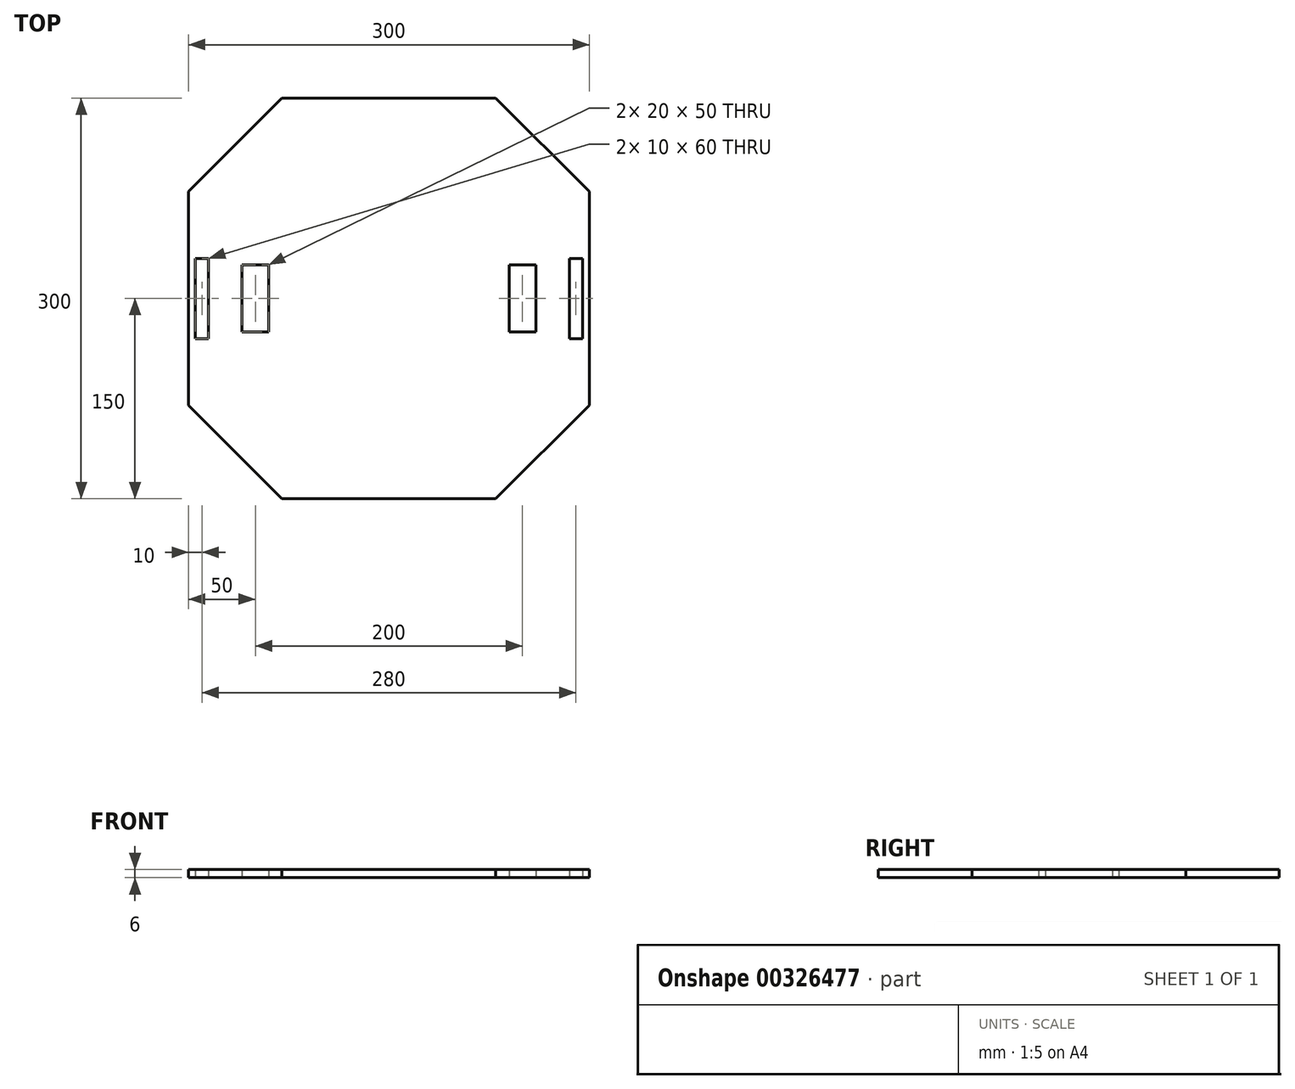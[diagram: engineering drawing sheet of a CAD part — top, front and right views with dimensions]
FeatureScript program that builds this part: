
annotation { "Feature Type Name" : "Feature", "Feature Type Description" : "" }
export const myFeature = defineFeature(function(context is Context, id is Id, definition is map)
    precondition{}
    {
        {
            var Q0;
            Q0=qCreatedBy(makeId("Top.planeOp"),FACE);
            var sketch = newSketch(context, id + "F0", { "sketchPlane" : qUnion([Q0])});
            skLineSegment(sketch, "E0.bottom", {"start": v(-150, 150) * mm, "end": v(150, 150) * mm});
            skLineSegment(sketch, "E0.top", {"start": v(-150, -150) * mm, "end": v(150, -150) * mm});
            skLineSegment(sketch, "E0.left", {"start": v(-150, 150) * mm, "end": v(-150, -150) * mm});
            skLineSegment(sketch, "E0.right", {"start": v(150, 150) * mm, "end": v(150, -150) * mm});
            skPoint(sketch, "E0.middle", {"position": v(0, 0) * mm});
            skLineSegment(sketch, "E1", {"start": v(-150, 80) * mm, "end": v(-80, 150) * mm});
            skLineSegment(sketch, "E2", {"start": v(0, 168.75) * mm, "end": v(0, -234.48) * mm});
            skPoint(sketch, "E2.startSnap0", {"position": v(0, 150) * mm});
            skPoint(sketch, "E2.endSnap0", {"position": v(0, -150) * mm});
            skLineSegment(sketch, "E3.MirrorCS", {"start": v(150, 80) * mm, "end": v(80, 150) * mm});
            skLineSegment(sketch, "E4", {"start": v(-191.93, 0) * mm, "end": v(243.46, 0) * mm});
            skPoint(sketch, "E4.startSnap0", {"position": v(-150, 0) * mm});
            skPoint(sketch, "E4.endSnap0", {"position": v(150, 0) * mm});
            skLineSegment(sketch, "E5.MirrorCS", {"start": v(150, -80) * mm, "end": v(80, -150) * mm});
            skLineSegment(sketch, "E6.MirrorCS", {"start": v(-150, -80) * mm, "end": v(-80, -150) * mm});
            skLineSegment(sketch, "E7.bottom", {"start": v(-110, 25) * mm, "end": v(-90, 25) * mm});
            skLineSegment(sketch, "E7.top", {"start": v(-110, -25) * mm, "end": v(-90, -25) * mm});
            skLineSegment(sketch, "E7.left", {"start": v(-110, 25) * mm, "end": v(-110, -25) * mm});
            skLineSegment(sketch, "E7.right", {"start": v(-90, 25) * mm, "end": v(-90, -25) * mm});
            skLineSegment(sketch, "E8.bottom", {"start": v(-145, 30) * mm, "end": v(-135, 30) * mm});
            skLineSegment(sketch, "E8.top", {"start": v(-145, -30) * mm, "end": v(-135, -30) * mm});
            skLineSegment(sketch, "E8.left", {"start": v(-145, 30) * mm, "end": v(-145, -30) * mm});
            skLineSegment(sketch, "E8.right", {"start": v(-135, 30) * mm, "end": v(-135, -30) * mm});
            skLineSegment(sketch, "E9.MirrorCS", {"start": v(110, 25) * mm, "end": v(90, 25) * mm});
            skLineSegment(sketch, "E10.MirrorCS", {"start": v(90, 25) * mm, "end": v(90, -25) * mm});
            skLineSegment(sketch, "E11.MirrorCS", {"start": v(110, 25) * mm, "end": v(110, -25) * mm});
            skLineSegment(sketch, "E12.MirrorCS", {"start": v(135, 30) * mm, "end": v(135, -30) * mm});
            skLineSegment(sketch, "E13.MirrorCS", {"start": v(145, 30) * mm, "end": v(135, 30) * mm});
            skLineSegment(sketch, "E14.MirrorCS", {"start": v(145, 30) * mm, "end": v(145, -30) * mm});
            skLineSegment(sketch, "E15.MirrorCS", {"start": v(145, -30) * mm, "end": v(135, -30) * mm});
            skLineSegment(sketch, "E16.MirrorCS", {"start": v(110, -25) * mm, "end": v(90, -25) * mm});
            skSolve(sketch);
        }
        {
            var Q0;
            {var subQ0=sQuery(id+"F0.wireOp",EDGE,"E3.MirrorCS");Q0=makeQuery(id+"F0.imprint","IMPRINT",FACE,{"disambiguationData":[TD([[makeQuery(id+"F0.imprint","IMPRINT",EDGE,{"derivedFrom":subQ0}),1.0]])]});}
            var Q1;
            {var subQ5=sQuery(id+"F0.wireOp",EDGE,"E1");Q1=makeQuery(id+"F0.imprint","IMPRINT",FACE,{"disambiguationData":[TD([[makeQuery(id+"F0.imprint","IMPRINT",EDGE,{"derivedFrom":subQ5}),-1.0]])]});}
            var Q2;
            {var subQ7=sQuery(id+"F0.wireOp",EDGE,"E6.MirrorCS");Q2=makeQuery(id+"F0.imprint","IMPRINT",FACE,{"disambiguationData":[TD([[makeQuery(id+"F0.imprint","IMPRINT",EDGE,{"derivedFrom":subQ7}),1.0]])]});}
            var Q3;
            {var subQ5=sQuery(id+"F0.wireOp",EDGE,"E5.MirrorCS");Q3=makeQuery(id+"F0.imprint","IMPRINT",FACE,{"disambiguationData":[TD([[makeQuery(id+"F0.imprint","IMPRINT",EDGE,{"derivedFrom":subQ5}),-1.0]])]});}
            extrude(context, id + "F1", {"entities" : qUnion([Q0, Q1, Q2, Q3]), "depth" : 6 * mm});
        }
    });
